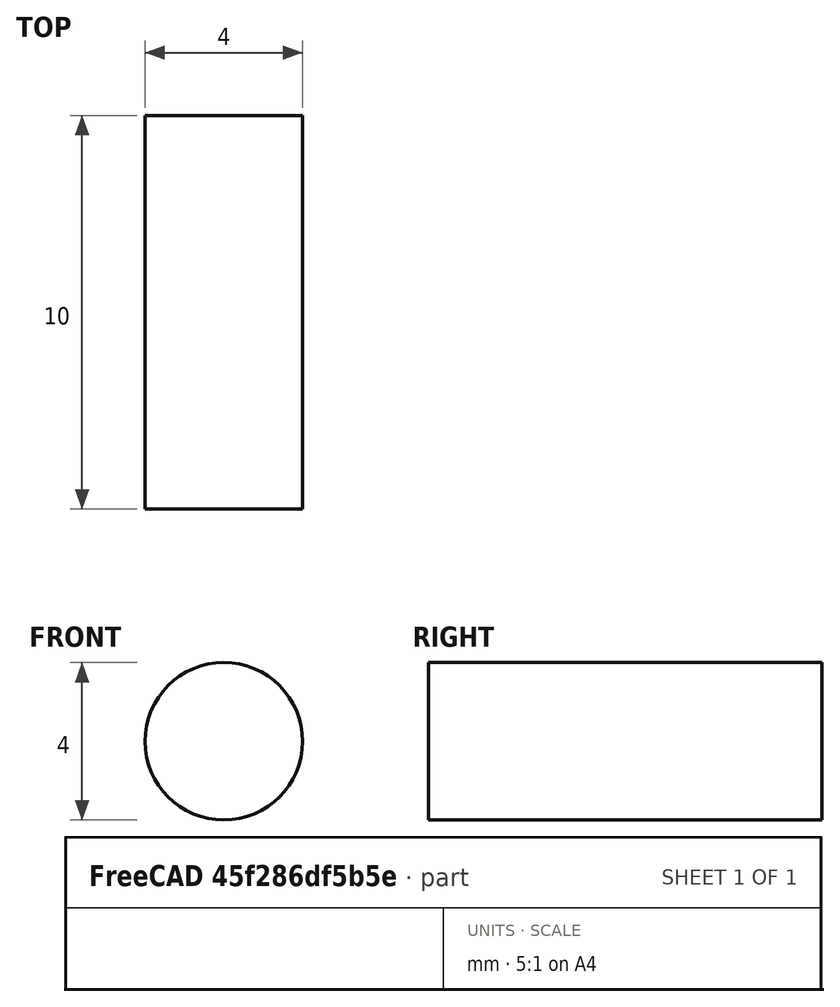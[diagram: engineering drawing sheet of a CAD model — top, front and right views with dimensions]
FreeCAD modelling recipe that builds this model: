
FCSTD DOCUMENT
Label: antenna_mount
License: CC-BY 3.0
LicenseURL: http://creativecommons.org/licenses/by/3.0/
objects: Part::Cylinder×1, Sketcher::SketchObject×1
note: 2 computed .brp shape members not serialized (recipe doc carries the construction recipe); baked Part::Feature solids carry a one-line shape summary decoded from their .brp

FEATURE [Part::Cylinder] Cylinder
  Angle = 360
  Height = 10
  Placement = pos=(0,0,0) rot=(1,0,0;1.5708rad)
  Radius = 2
FEATURE [Sketcher::SketchObject] Sketch
  Placement = pos=(0,-10,0) rot=(1,0,0;1.5708rad)
  Support = -> Cylinder [Face2]
  sketch-geometry (18):
    g0: GeomPoint [constr] X=-22 Y=0 Z=0
    g1: LineSegment StartX=-21 StartY=-37.5278 StartZ=0 EndX=-10.6506 EndY=-31.5526 EndZ=0
    g2: LineSegment StartX=-19.0526 StartY=-11 StartZ=0 EndX=-9.55255 EndY=-27.4545 EndZ=0
    g3: LineSegment [constr] StartX=-12.6202 StartY=15.1569 StartZ=0 EndX=7.116 EndY=18.3946 EndZ=0
    g4: LineSegment [constr] StartX=7.116 StartY=18.3946 StartZ=0 EndX=15.8579 EndY=-34.8931 EndZ=0
    g5: LineSegment [constr] StartX=15.8579 StartY=-34.8931 StartZ=0 EndX=-3.87825 EndY=-38.1308 EndZ=0
    g6: LineSegment [constr] StartX=-3.87825 StartY=-38.1308 StartZ=0 EndX=-12.6202 EndY=15.1569 EndZ=0
    g7: ArcOfCircle [constr] CenterX=0 CenterY=0 CenterZ=0 NormalX=0 NormalY=0 NormalZ=1 Radius=19.7231 StartAngle=1.20168 EndAngle=2.26512
    g8: GeomPoint [constr] X=-2.75209 Y=16.7758 Z=0
    g9: ArcOfCircle CenterX=-12.1506 CenterY=-28.9545 CenterZ=0 NormalX=0 NormalY=0 NormalZ=1 Radius=3 StartAngle=5.23599 EndAngle=6.80678
    g10: Circle [constr] CenterX=-7.8205 CenterY=-26.4545 CenterZ=0 NormalX=0 NormalY=0 NormalZ=1 Radius=2
    g11: LineSegment StartX=-4.5606e-08 StartY=22 StartZ=0 EndX=53 EndY=22 EndZ=0
    g12: ArcOfCircle CenterX=0 CenterY=0 CenterZ=0 NormalX=0 NormalY=0 NormalZ=1 Radius=22 StartAngle=1.5708 EndAngle=3.66519
    g13: LineSegment StartX=-22 StartY=-39.2598 StartZ=0 EndX=-22 EndY=-40.2598 EndZ=0
    g14: ArcOfCircle CenterX=-20 CenterY=-39.2598 CenterZ=0 NormalX=0 NormalY=0 NormalZ=1 Radius=2 StartAngle=2.0944 EndAngle=3.14159
    g15: LineSegment StartX=-22 StartY=-40.2598 StartZ=0 EndX=53 EndY=-40.2598 EndZ=0
    g16: LineSegment StartX=53 StartY=22 StartZ=0 EndX=53 EndY=-40.2598 EndZ=0
    g17: Circle [constr] CenterX=0 CenterY=0 CenterZ=0 NormalX=0 NormalY=0 NormalZ=1 Radius=10.5
  constraints (48):
    c: Distance(g-1,g0) = 22
    c: DistanceY(g-1,g0) = 0
    c: Perpendicular(g2,g1)
    c: Coincident(g3,g4)
    c: Coincident(g4,g5)
    c: Coincident(g5,g6)
    c: Coincident(g6,g3)
    c: Distance(g4,g5) = 20
    c: Distance(g3,g4) = 54
    c: Perpendicular(g3,g6)
    c: Perpendicular(g6,g5)
    c: Perpendicular(g5,g4)
    c: Coincident(g7,g3)
    c: Coincident(g7,g3)
    c: PointOnObject(g8,g3)
    c: Distance(g8,g3) = 10
    c: Distance(g7,g8) = 17
    c: Coincident(g7,g-1)
    c: Tangent(g1,g9)
    c: Tangent(g2,g9)
    c: Radius(g9) = 3
    c: Radius(g10) = 2
    c: Tangent(g10,g6)
    c: Tangent(g10,g9)
    c: Tangent(g10,g2)
    c: Radius(g12) = 22
    c: Coincident(g12,g-1)
    c: Coincident(g12,g2)
    c: Tangent(g2,g12)
    c: Horizontal(g11)
    c: Coincident(g11,g12)
    c: Tangent(g11,g12)
    c: Tangent(g1,g12)
    c: Vertical(g13)
    c: Tangent(g1,g14)
    c: Tangent(g13,g14)
    c: DistanceX(g-1,g13) = -22
    c: Radius(g14) = 2
    c: DistanceY(g13) = -1
    c: Horizontal(g15)
    c: Coincident(g15,g13)
    c: Distance(g15) = 75
    c: DistanceX(g15,g11) = 0
    c: Angle(g1) = 0.523599
    c: Coincident(g16,g11)
    c: Coincident(g16,g15)
    c: Radius(g17) = 10.5
    c: Coincident(g17,g-1)
